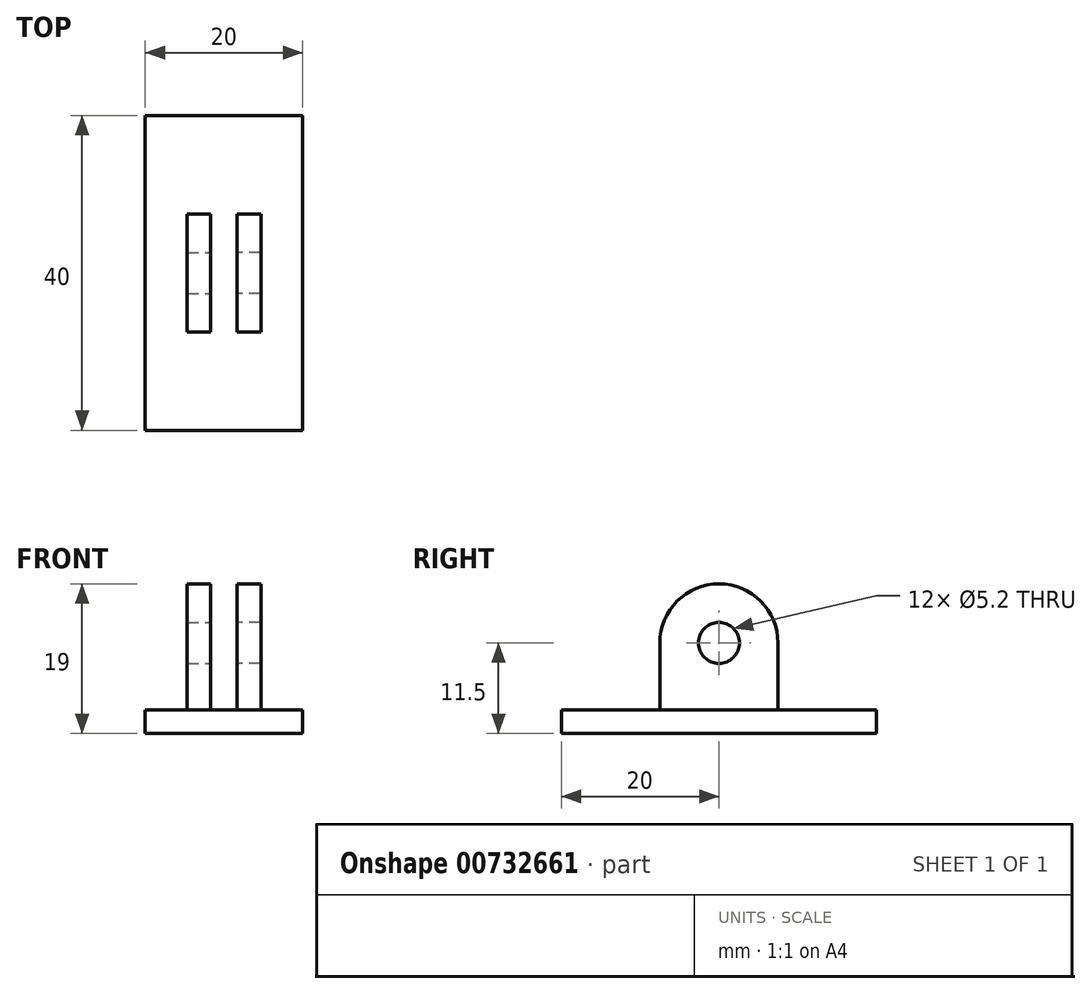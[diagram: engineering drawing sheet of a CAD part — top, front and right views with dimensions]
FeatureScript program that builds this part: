
annotation { "Feature Type Name" : "Feature", "Feature Type Description" : "" }
export const myFeature = defineFeature(function(context is Context, id is Id, definition is map)
    precondition{}
    {
        {
            var Q0;
            Q0=qCreatedBy(makeId("Right.planeOp"),FACE);
            cPlane(context, id + "F0", {"entities" : qUnion([Q0]), "cplaneType" : CPlaneType.OFFSET, "offset" : (3.4 / 2) * mm, "width" : 150 * mm, "height" : 150 * mm});
        }
        {
            var Q0;
            Q0=qCreatedBy(id+"F0.planeOp",FACE);
            var sketch = newSketch(context, id + "F1", { "sketchPlane" : qUnion([Q0])});
            skLineSegment(sketch, "E0", {"start": v(0, 0) * mm, "end": v(0, 8.5) * mm, "construction": true});
            skCircle(sketch, "E1", {"center": v(0, 8.5) * mm, "radius": 2.6 * mm});
            skArc(sketch, "E2", {"start": v(7.5, 8.5) * mm, "mid": v(0, 16) * mm, "end": v(-7.5, 8.5) * mm});
            skLineSegment(sketch, "E3", {"start": v(0, 8.5) * mm, "end": v(-7.5, 8.5) * mm, "construction": true});
            skLineSegment(sketch, "E4", {"start": v(-7.5, 8.5) * mm, "end": v(-7.5, 0) * mm});
            skLineSegment(sketch, "E5.MirrorCS", {"start": v(7.5, 8.5) * mm, "end": v(7.5, 0) * mm});
            skLineSegment(sketch, "E6", {"start": v(-7.5, 0) * mm, "end": v(7.5, 0) * mm});
            skSolve(sketch);
        }
        {
            var Q0;
            Q0=qSketchRegion(id+"F1",true);
            extrude(context, id + "F2", {"entities" : qUnion([Q0]), "depth" : 3 * mm});
        }
        {
            var Q0;
            Q0=makeQuery(id+"F2.opExtrude","SWEPT_BODY",BODY,{"disambiguationData":[OSD([sQuery(id+"F1.wireOp",EDGE,"E1"),sQuery(id+"F1.wireOp",EDGE,"E2"),sQuery(id+"F1.wireOp",EDGE,"E4"),sQuery(id+"F1.wireOp",EDGE,"E5.MirrorCS"),sQuery(id+"F1.wireOp",EDGE,"E6")])]});
            var Q1;
            Q1=makeQuery(id+"F2.opExtrude","CAP_FACE",FACE,{"disambiguationData":[OSD([sQuery(id+"F1.wireOp",EDGE,"E1"),sQuery(id+"F1.wireOp",EDGE,"E2"),sQuery(id+"F1.wireOp",EDGE,"E4"),sQuery(id+"F1.wireOp",EDGE,"E5.MirrorCS"),sQuery(id+"F1.wireOp",EDGE,"E6")])],"isStart":true});
            var Q2;
            Q2=qCreatedBy(makeId("Right.planeOp"),FACE);
            mirror(context, id + "F3", {"entities" : qUnion([Q0]), "faces" : qUnion([Q1]), "mirrorPlane" : qUnion([Q2])});
        }
        {
            var Q0;
            Q0=qCreatedBy(makeId("Top.planeOp"),FACE);
            var sketch = newSketch(context, id + "F4", { "sketchPlane" : qUnion([Q0])});
            skLineSegment(sketch, "E7.bottom", {"start": v(10, -20) * mm, "end": v(-10, -20) * mm});
            skLineSegment(sketch, "E7.top", {"start": v(10, 20) * mm, "end": v(-10, 20) * mm});
            skLineSegment(sketch, "E7.left", {"start": v(10, -20) * mm, "end": v(10, 20) * mm});
            skLineSegment(sketch, "E7.right", {"start": v(-10, -20) * mm, "end": v(-10, 20) * mm});
            skPoint(sketch, "E7.middle", {"position": v(0, 0) * mm});
            skSolve(sketch);
        }
        {
            var Q0;
            Q0=qSketchRegion(id+"F4",true);
            extrude(context, id + "F5", {"entities" : qUnion([Q0]), "oppositeDirection" : true, "depth" : 3 * mm});
        }
    });
